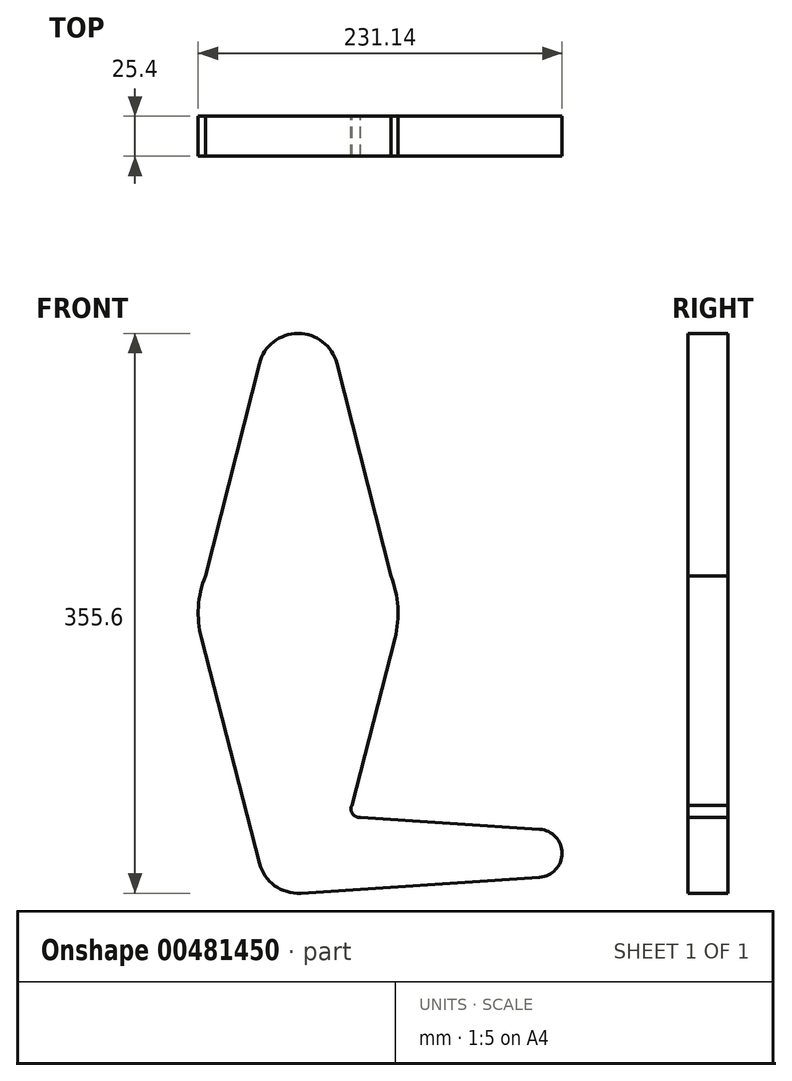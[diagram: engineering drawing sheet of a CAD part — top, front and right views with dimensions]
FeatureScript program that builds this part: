
annotation { "Feature Type Name" : "Feature", "Feature Type Description" : "" }
export const myFeature = defineFeature(function(context is Context, id is Id, definition is map)
    precondition{}
    {
        {
            var Q0;
            Q0=qCreatedBy(makeId("Front.planeOp"),FACE);
            var sketch = newSketch(context, id + "F0", { "sketchPlane" : qUnion([Q0])});
            skCircle(sketch, "E0", {"center": v(0, 0) * mm, "radius": 25.4 * mm});
            skLineSegment(sketch, "E1", {"start": v(0, 0) * mm, "end": v(0, 152.4) * mm, "construction": true});
            skLineSegment(sketch, "E2", {"start": v(0, 152.4) * mm, "end": v(0, 304.8) * mm, "construction": true});
            skLineSegment(sketch, "E3", {"start": v(0, 0) * mm, "end": v(152.4, 0) * mm, "construction": true});
            skCircle(sketch, "E4", {"center": v(0, 152.4) * mm, "radius": 63.5 * mm});
            skCircle(sketch, "E5", {"center": v(0, 304.8) * mm, "radius": 25.4 * mm});
            skCircle(sketch, "E6", {"center": v(152.4, 0) * mm, "radius": 15.24 * mm});
            skLineSegment(sketch, "E7", {"start": v(-58.93, 176.06) * mm, "end": v(-24.62, 311.06) * mm});
            skLineSegment(sketch, "E8", {"start": v(-24.6, -6.35) * mm, "end": v(-61.48, 136.53) * mm});
            skLineSegment(sketch, "E9.MirrorCS", {"start": v(58.93, 176.06) * mm, "end": v(24.62, 311.06) * mm});
            skLineSegment(sketch, "E10", {"start": v(39.53, 22.82) * mm, "end": v(153.42, 15.2) * mm});
            skLineSegment(sketch, "E11", {"start": v(1.7, -25.34) * mm, "end": v(153.42, -15.2) * mm});
            skLineSegment(sketch, "E12.trimOffspring", {"start": v(34.1, 30.44) * mm, "end": v(61.48, 136.53) * mm});
            skArc(sketch, "E13", {"start": v(34.1, 30.44) * mm, "mid": v(34.58, 25.03) * mm, "end": v(39.53, 22.82) * mm});
            skPoint(sketch, "E14.MirrorCS.start.orphan", {"position": v(24.6, -6.35) * mm});
            skSolve(sketch);
        }
        {
            var Q0;
            Q0 = qSketchRegion(id + "F0", true);
            extrude(context, id + "F1", {"entities" : qUnion([Q0]), "depth" : 25.4 * mm});
        }
    });
